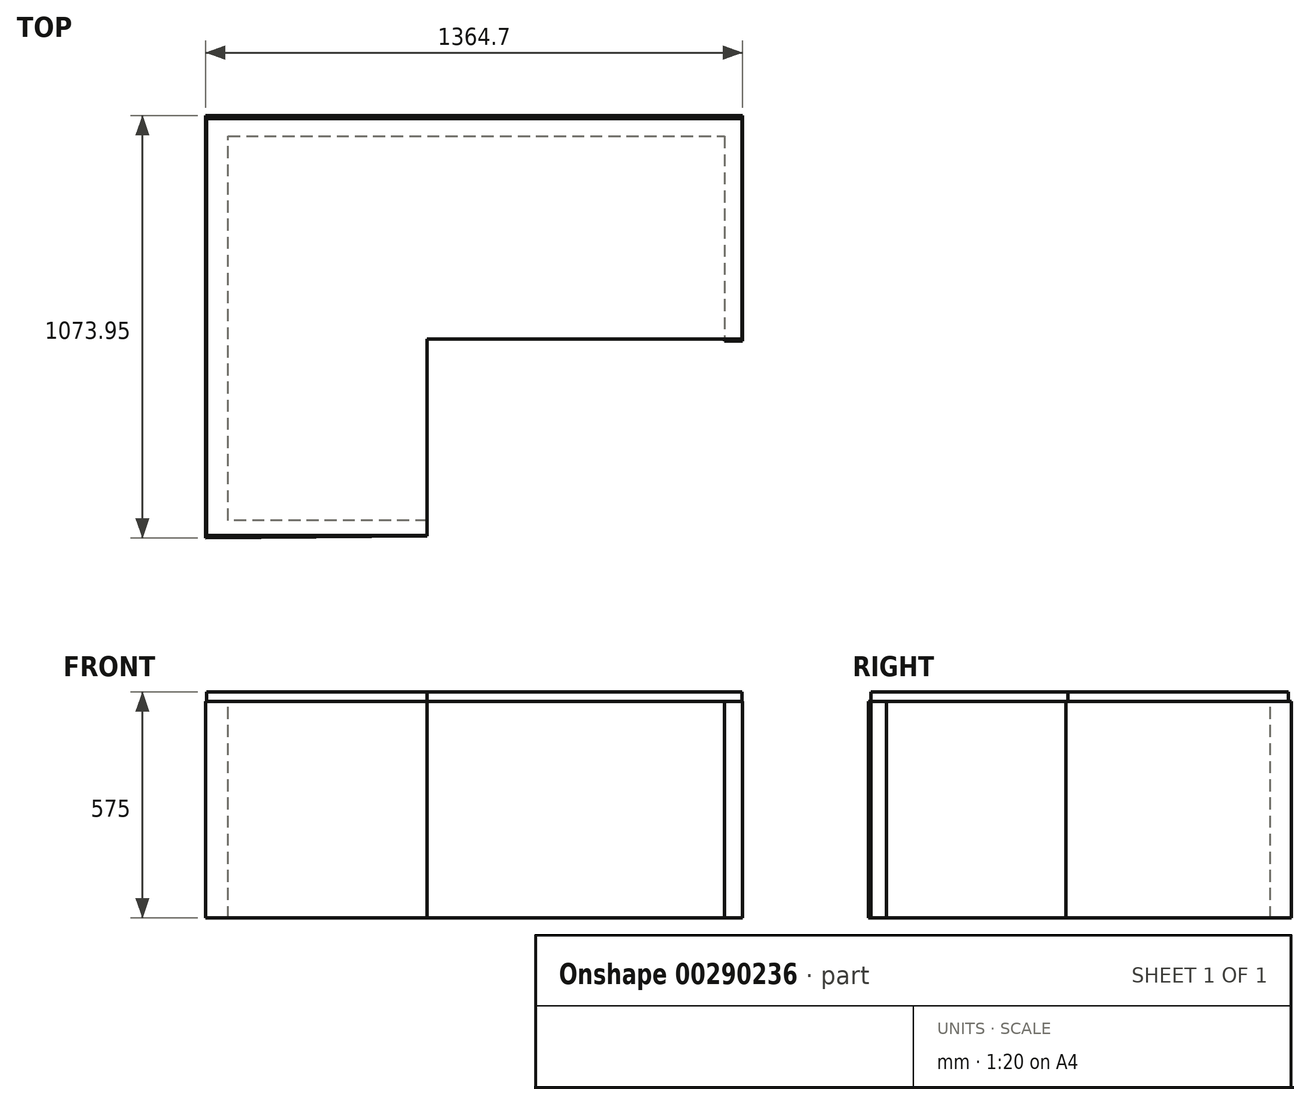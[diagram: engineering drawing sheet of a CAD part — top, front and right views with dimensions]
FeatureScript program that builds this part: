
annotation { "Feature Type Name" : "Feature", "Feature Type Description" : "" }
export const myFeature = defineFeature(function(context is Context, id is Id, definition is map)
    precondition{}
    {
        {
            var Q0;
            Q0=qCreatedBy(makeId("Top.planeOp"),FACE);
            var sketch = newSketch(context, id + "F0", { "sketchPlane" : qUnion([Q0])});
            skLineSegment(sketch, "E0", {"start": v(-681.2, 513.32) * mm, "end": v(678.8, 513.32) * mm});
            skLineSegment(sketch, "E1", {"start": v(678.8, 513.32) * mm, "end": v(678.8, -46.68) * mm});
            skLineSegment(sketch, "E2", {"start": v(678.8, -46.68) * mm, "end": v(-121.2, -46.68) * mm});
            skLineSegment(sketch, "E3", {"start": v(-121.2, -46.68) * mm, "end": v(-121.2, -546.68) * mm});
            skLineSegment(sketch, "E4", {"start": v(-121.2, -546.68) * mm, "end": v(-681.2, -546.68) * mm});
            skLineSegment(sketch, "E5", {"start": v(-681.2, -546.68) * mm, "end": v(-681.2, 513.32) * mm});
            skSolve(sketch);
        }
        {
            var Q0;
            Q0 = qSketchRegion(id + "F0", true);
            extrude(context, id + "F1", {"entities" : qUnion([Q0]), "depth" : 25 * mm});
        }
        {
            var Q0;
            Q0=makeQuery(id+"F0.imprint","IMPRINT",FACE,{"disambiguationData":[TD([[makeQuery(id+"F0.imprint","IMPRINT",EDGE,{"derivedFrom":sQuery(id+"F0.wireOp",EDGE,"E0")}),-1.0]])]});
            var sketch = newSketch(context, id + "F2", { "sketchPlane" : qUnion([Q0])});
            skLineSegment(sketch, "E6", {"start": v(-121.49, -547.14) * mm, "end": v(-121.49, -507.62) * mm});
            skLineSegment(sketch, "E7", {"start": v(-121.49, -507.62) * mm, "end": v(-626.58, -507.62) * mm});
            skLineSegment(sketch, "E8", {"start": v(-626.58, -507.62) * mm, "end": v(-626.58, 468.02) * mm});
            skLineSegment(sketch, "E9", {"start": v(-626.58, 468.02) * mm, "end": v(634.54, 468.02) * mm});
            skLineSegment(sketch, "E10", {"start": v(634.54, 468.02) * mm, "end": v(634.54, -51.7) * mm});
            skLineSegment(sketch, "E11", {"start": v(634.54, -51.7) * mm, "end": v(679.96, -51.7) * mm});
            skLineSegment(sketch, "E12", {"start": v(679.96, -51.7) * mm, "end": v(679.96, 520.71) * mm});
            skLineSegment(sketch, "E13", {"start": v(679.96, 520.71) * mm, "end": v(-684.74, 520.71) * mm});
            skLineSegment(sketch, "E14", {"start": v(-684.74, 520.71) * mm, "end": v(-684.74, -553.24) * mm});
            skLineSegment(sketch, "E15", {"start": v(-684.74, -553.24) * mm, "end": v(-121.49, -547.14) * mm});
            skSolve(sketch);
        }
        {
            var Q0;
            Q0 = qSketchRegion(id + "F2", true);
            extrude(context, id + "F3", {"entities" : qUnion([Q0]), "operationType" : NewBodyOperationType.ADD, "oppositeDirection" : true, "depth" : 550 * mm, "offsetDistance" : 25 * mm});
        }
    });
